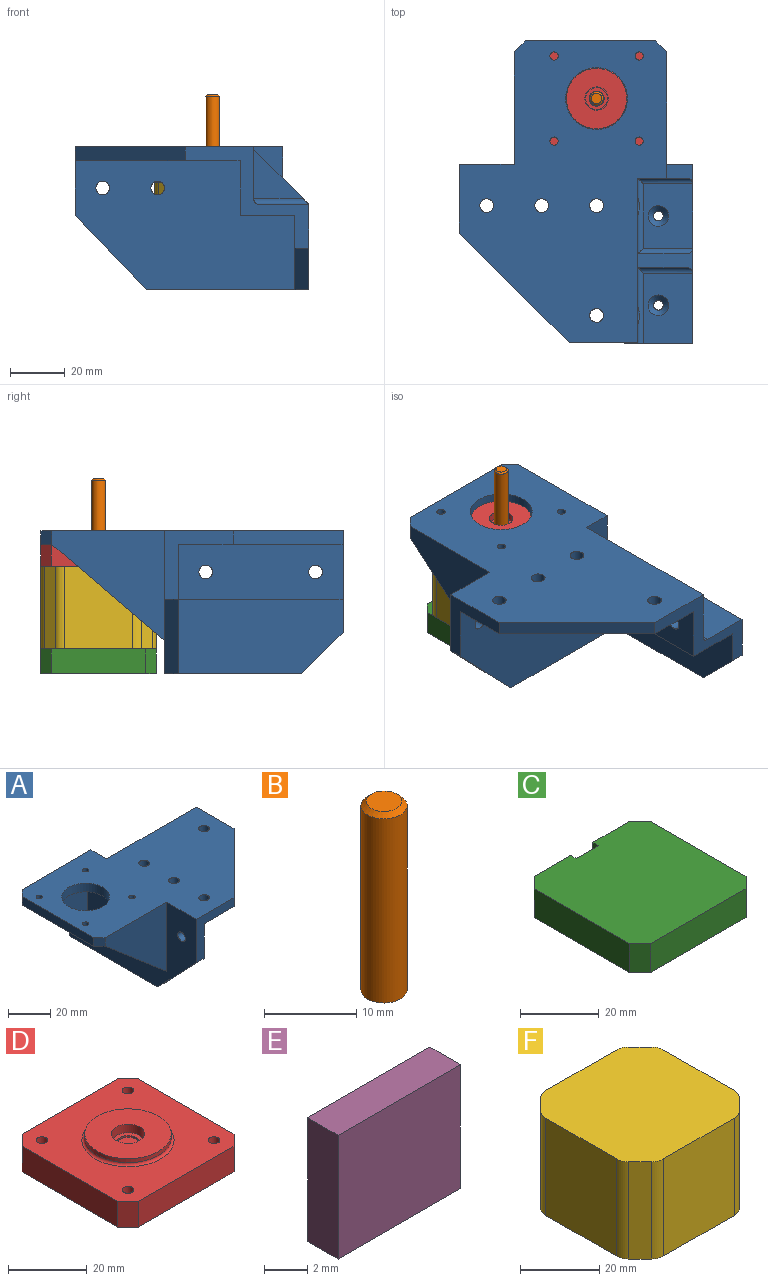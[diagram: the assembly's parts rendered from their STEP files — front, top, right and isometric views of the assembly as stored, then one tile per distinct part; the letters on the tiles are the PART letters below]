
ASSEMBLY  parts=6 mates=6
PART A: 56 faces, bbox 110x85x52 mm
  f0: cylinder r=2mm len=27.5mm, axis (1,0,0), area 73.4mm2, adj f6,f39,f49,f50,f54
  f1: cylinder r=2mm len=27.5mm, axis (1,0,0), area 75.7mm2, adj f3,f5,f6,f51,f53
  f2: plane 65x31mm, normal (0,1,0), area 1902.5mm2, adj f3,f5,f10,f24,f39,f41,f42,f52
  f3: plane 45x37mm, normal (1,0,0), area 365.9mm2, adj f1,f2,f4,f5,f6,f9,f21,f36
  f4: plane 60x27mm, normal (0,-1,0), area 1507.5mm2, adj f3,f8,f10,f38,f52
  f5: plane 25.5x18mm, normal (0,0,1), area 414.8mm2, adj f1,f2,f3,f48,f51
  f6: plane 60x20.5mm, normal (0,1,0), area 1026.3mm2, adj f0,f1,f3,f16,f21,f33,f37,f42
  f7: plane 46x40mm, normal (0,1,0), area 980mm2, adj f21,f24,f26,f32,f37,f41
  f8: plane 80x47mm, normal (1,0,0), area 2970.8mm2, adj f4,f9,f10,f11,f15,f17,f22,f36
  f9: plane 60x20mm, normal (0,-1,0), area 1160.7mm2, adj f3,f8,f16,f33,f36,f38
  f10: plane 59.08x50mm, normal (0,0,-1), area 520.4mm2, adj f2,f4,f8,f11,f24,f52
  f11: plane 27x25.92mm, normal (0,-0.72,-0.69), area 187.1mm2, adj f8,f10,f17,f24
  f12: plane 55.5x45mm, normal (0,0,-1), area 1809.6mm2, adj f13,f19,f23,f24,f25,f26,f27,f28
  f13: cylinder r=1.5mm len=5mm, axis (0,0,1), area 47.1mm2, adj f12,f21
  f14: cylinder r=2.5mm len=5mm, axis (0,0,1), area 78.5mm2, adj f21,f36
  f15: cylinder r=2.5mm len=5mm, axis (1,0,0), area 78.5mm2, adj f8,f24
  f16: cylinder r=2.5mm len=5mm, axis (0,-1,0), area 78.5mm2, adj f6,f9
  f17: plane 25x25mm, normal (0,-1,0), area 225mm2, adj f8,f11,f21,f24,f36,f40
  f18: plane 41x40mm, normal (0,-1,0), area 922.5mm2, adj f19,f21,f24,f31
  f19: plane 5x4mm, normal (-0.71,-0.71,0), area 28.3mm2, adj f12,f18,f21,f30
  f20: cylinder r=2.5mm len=5mm, axis (0,0,1), area 78.5mm2, adj f21,f36
  f21: plane 110x75.5mm, normal (0,0,1), area 5454.6mm2, adj f3,f6,f7,f13,f14,f17,f18,f19
  f22: cylinder r=2.5mm len=5mm, axis (1,0,0), area 78.5mm2, adj f8,f24
  f23: cylinder r=1.5mm len=5mm, axis (0,0,1), area 47.1mm2, adj f12,f21
  f24: plane 85x52mm, normal (-1,0,0), area 3388.9mm2, adj f2,f7,f10,f11,f12,f15,f17,f18
  f25: plane 41x35mm, normal (0,-1,0), area 717.5mm2, adj f12,f24,f32
  f26: plane 5x4mm, normal (-0.71,0.71,0), area 28.3mm2, adj f7,f12,f21,f30
  f27: cylinder r=11.25mm len=22.5mm, axis (0,0,1), area 353.4mm2, adj f12,f21
  f28: plane 41x35mm, normal (0,1,0), area 717.5mm2, adj f12,f24,f31
  f29: cylinder r=1.5mm len=5mm, axis (0,0,1), area 47.1mm2, adj f12,f21
  f30: plane 47.5x5mm, normal (-1,0,0), area 237.5mm2, adj f12,f19,f21,f26
  f31: plane 41x35mm, normal (-0.65,0,-0.76), area 161.7mm2, adj f12,f18,f24,f28
  f32: plane 41x35mm, normal (-0.65,0,-0.76), area 161.7mm2, adj f7,f12,f24,f25
  f33: cylinder r=2.5mm len=5mm, axis (0,-1,0), area 78.5mm2, adj f6,f9
  f34: cylinder r=2.5mm len=5mm, axis (0,0,1), area 78.5mm2, adj f21,f36
  f35: cylinder r=1.5mm len=5mm, axis (0,0,1), area 47.1mm2, adj f12,f21
  f36: plane 60x60mm, normal (0,0,-1), area 2721.5mm2, adj f3,f8,f9,f14,f17,f20,f34,f40
  f37: plane 19x18mm, normal (1,0,0), area 227.6mm2, adj f6,f7,f21,f41,f50
  f38: plane 60x20mm, normal (0,0,-1), area 1180.8mm2, adj f3,f4,f8,f9,f45,f46
  f39: plane 23.5x18mm, normal (0,0,1), area 378.8mm2, adj f0,f2,f47,f49,f50
  f40: plane 40x40mm, normal (0.71,-0.71,0), area 282.8mm2, adj f3,f17,f21,f36
  f41: plane 9.5x9.5mm, normal (0,0.71,0.71), area 68.4mm2, adj f2,f7,f24,f37,f50
  f42: plane 20x20mm, normal (0,0.71,0.71), area 143.8mm2, adj f2,f6,f43,f44,f49,f51
  f43: plane 18x18mm, normal (-1,0,0), area 162mm2, adj f6,f42,f49
  f44: plane 18x18mm, normal (1,0,0), area 162mm2, adj f6,f42,f51
  f45: cylinder r=1.75mm len=3.5mm, axis (0,0,1), area 22mm2, adj f38,f47
  f46: cylinder r=1.75mm len=3.5mm, axis (0,0,1), area 22mm2, adj f38,f48
  f47: cone r=1.75mm half-angle=45deg, axis (0,0,1), area 48.9mm2, adj f39,f45
  f48: cone r=1.75mm half-angle=45deg, axis (0,0,1), area 48.9mm2, adj f5,f46
  f49: cylinder r=2mm len=20mm, axis (0,1,0), area 58.3mm2, adj f0,f39,f42,f43
  f50: cylinder r=2mm len=20mm, axis (0,1,0), area 58.3mm2, adj f0,f37,f39,f41
  f51: cylinder r=2mm len=20mm, axis (0,-1,0), area 58.3mm2, adj f1,f5,f42,f44
  f52: plane 15x15mm, normal (0.71,0,-0.71), area 106.1mm2, adj f2,f3,f4,f10
  f53: cylinder r=5.5mm len=7.55mm, axis (0,-1,0), area 2.8mm2, adj f1,f6
  f54: cylinder r=5.5mm len=7.55mm, axis (0,-1,0), area 2.8mm2, adj f0,f6
  f55: cylinder r=2.5mm len=5mm, axis (0,0,1), area 78.5mm2, adj f21,f36
PART B: 4 faces, bbox 5x5x25 mm
  f0: cone r=1.93mm half-angle=45deg, axis (0,0,-1), area 11.3mm2, adj f1,f3
  f1: cylinder r=2.5mm len=24.43mm, axis (0,0,-1), area 383.7mm2, adj f0,f2
  f2: plane 5x5mm, normal (0,0,-1), area 19.6mm2, adj f1
  f3: plane 3.85x3.85mm, normal (0,0,1), area 11.6mm2, adj f0
PART C: 14 faces, bbox 42x42x9 mm
  f0: plane 34.37x9mm, normal (0,1,0), area 253.3mm2, adj f1,f7,f8,f9,f10,f11,f12
  f1: plane 9x3.82mm, normal (0.71,0.71,0), area 48.6mm2, adj f0,f2,f8,f9
  f2: plane 34.37x9mm, normal (1,0,0), area 309.3mm2, adj f1,f3,f8,f9
  f3: plane 9x3.82mm, normal (0.71,-0.71,0), area 48.6mm2, adj f2,f4,f8,f9
  f4: plane 34.37x9mm, normal (0,-1,0), area 309.3mm2, adj f3,f5,f8,f9
  f5: plane 9x3.82mm, normal (-0.71,-0.71,0), area 48.6mm2, adj f4,f6,f8,f9
  f6: plane 34.37x9mm, normal (-1,0,0), area 309.3mm2, adj f5,f7,f8,f9
  f7: plane 9x3.82mm, normal (-0.71,0.71,0), area 48.6mm2, adj f0,f6,f8,f9
  f8: plane 42x42mm, normal (0,0,-1), area 1734.9mm2, adj f0,f1,f2,f3,f4,f5,f6,f7
  f9: plane 42x42mm, normal (0,0,1), area 1718.9mm2, adj f0,f1,f2,f3,f4,f5,f6,f7
  f10: plane 7x2mm, normal (1,0,0), area 14mm2, adj f0,f9,f11,f13
  f11: plane 8x2mm, normal (0,0,1), area 16mm2, adj f0,f10,f12,f13
  f12: plane 7x2mm, normal (-1,0,0), area 14mm2, adj f0,f9,f11,f13
  f13: plane 8x7mm, normal (0,1,0), area 56mm2, adj f9,f10,f11,f12
PART D: 27 faces, bbox 42x42x10 mm
  f0: torus R=11.75mm, axis (0,0,-1), area 83.4mm2, adj f4,f18
  f1: cylinder r=2.75mm len=5.5mm, axis (0,0,-1), area 8.6mm2, adj f25,f26
  f2: cylinder r=4mm len=8mm, axis (0,0,-1), area 12.6mm2, adj f24,f25
  f3: cylinder r=4.25mm len=8.5mm, axis (0,0,1), area 80.1mm2, adj f23,f24
  f4: cylinder r=11mm len=22mm, axis (0,0,-1), area 86.4mm2, adj f0,f23
  f5: cylinder r=1.5mm len=4.5mm, axis (0,0,1), area 42.4mm2, adj f18,f22
  f6: cylinder r=1.5mm len=4.5mm, axis (0,0,1), area 42.4mm2, adj f18,f21
  f7: cylinder r=1.5mm len=4.5mm, axis (0,0,1), area 42.4mm2, adj f18,f20
  f8: cylinder r=1.5mm len=4.5mm, axis (0,0,1), area 42.4mm2, adj f18,f19
  f9: plane 8x3.82mm, normal (0.71,0.71,0), area 43.2mm2, adj f10,f16,f17,f18
  f10: plane 34.37x8mm, normal (1,0,0), area 274.9mm2, adj f9,f11,f17,f18
  f11: plane 8x3.82mm, normal (0.71,-0.71,0), area 43.2mm2, adj f10,f12,f17,f18
  f12: plane 34.37x8mm, normal (0,-1,0), area 274.9mm2, adj f11,f13,f17,f18
  f13: plane 8x3.82mm, normal (-0.71,-0.71,0), area 43.2mm2, adj f12,f14,f17,f18
  f14: plane 34.37x8mm, normal (-1,0,0), area 274.9mm2, adj f13,f15,f17,f18
  f15: plane 8x3.82mm, normal (-0.71,0.71,0), area 43.2mm2, adj f14,f16,f17,f18
  f16: plane 34.37x8mm, normal (0,1,0), area 274.9mm2, adj f9,f15,f17,f18
  f17: plane 42x42mm, normal (0,0,-1), area 1734.9mm2, adj f9,f10,f11,f12,f13,f14,f15,f16
  f18: plane 42x42mm, normal (0,0,1), area 1272.9mm2, adj f0,f5,f6,f7,f8,f9,f10,f11
  f19: plane 3x3mm, normal (0,0,1), area 7.1mm2, adj f8
  f20: plane 3x3mm, normal (0,0,1), area 7.1mm2, adj f7
  f21: plane 3x3mm, normal (0,0,1), area 7.1mm2, adj f6
  f22: plane 3x3mm, normal (0,0,1), area 7.1mm2, adj f5
  f23: plane 22x22mm, normal (0,0,1), area 323.4mm2, adj f3,f4
  f24: plane 8.5x8.5mm, normal (0,0,1), area 6.5mm2, adj f2,f3
  f25: plane 8x8mm, normal (0,0,1), area 26.5mm2, adj f1,f2
  f26: plane 5.5x5.5mm, normal (0,0,1), area 23.8mm2, adj f1
PART E: 11 faces, bbox 8x2x7 mm
  f0: plane 8x2mm, normal (0,0,-1), area 16mm2, adj f1,f3,f4,f9
  f1: plane 7x2mm, normal (-1,0,0), area 14mm2, adj f0,f2,f4,f9
  f2: plane 8x2mm, normal (0,0,1), area 16mm2, adj f1,f3,f4,f9
  f3: plane 7x2mm, normal (1,0,0), area 14mm2, adj f0,f2,f4,f9
  f4: plane 8x7mm, normal (0,-1,0), area 56mm2, adj f0,f1,f2,f3
  f5: plane 7.5x1.75mm, normal (0,0,-1), area 13.1mm2, adj f6,f8,f9,f10
  f6: plane 6.5x1.75mm, normal (-1,0,0), area 11.4mm2, adj f5,f7,f9,f10
  f7: plane 7.5x1.75mm, normal (0,0,1), area 13.1mm2, adj f6,f8,f9,f10
  f8: plane 6.5x1.75mm, normal (1,0,0), area 11.4mm2, adj f5,f7,f9,f10
  f9: plane 8x7mm, normal (0,1,0), area 7.3mm2, adj f0,f1,f2,f3,f5,f6,f7,f8
  f10: plane 7.5x6.5mm, normal (0,1,0), area 48.7mm2, adj f5,f6,f7,f8
PART F: 18 faces, bbox 42x42x30 mm
  f0: cylinder r=4.48mm len=30mm, axis (0,0,1), area 105.5mm2, adj f1,f15,f16,f17
  f1: plane 30x4.02mm, normal (0.71,-0.71,0), area 170.6mm2, adj f0,f2,f16,f17
  f2: cylinder r=4.48mm len=30mm, axis (0,0,1), area 105.5mm2, adj f1,f3,f16,f17
  f3: plane 30x25mm, normal (0,-1,0), area 750mm2, adj f2,f4,f16,f17
  f4: cylinder r=4.48mm len=30mm, axis (0,0,1), area 105.5mm2, adj f3,f5,f16,f17
  f5: plane 30x4.02mm, normal (-0.71,-0.71,0), area 170.6mm2, adj f4,f6,f16,f17
  f6: cylinder r=4.48mm len=30mm, axis (0,0,1), area 105.5mm2, adj f5,f7,f16,f17
  f7: plane 30x25mm, normal (-1,0,0), area 750mm2, adj f6,f8,f16,f17
  f8: cylinder r=4.48mm len=30mm, axis (0,0,1), area 105.5mm2, adj f7,f9,f16,f17
  f9: plane 30x4.02mm, normal (-0.71,0.71,0), area 170.6mm2, adj f8,f10,f16,f17
  f10: cylinder r=4.48mm len=30mm, axis (0,0,1), area 105.5mm2, adj f9,f11,f16,f17
  f11: plane 30x25mm, normal (0,1,0), area 750mm2, adj f10,f12,f16,f17
  f12: cylinder r=4.48mm len=30mm, axis (0,0,1), area 105.5mm2, adj f11,f13,f16,f17
  f13: plane 30x4.02mm, normal (0.71,0.71,0), area 170.6mm2, adj f12,f14,f16,f17
  f14: cylinder r=4.48mm len=30mm, axis (0,0,1), area 105.5mm2, adj f13,f15,f16,f17
  f15: plane 30x25mm, normal (1,0,0), area 750mm2, adj f0,f14,f16,f17
  f16: plane 42x42mm, normal (0,0,-1), area 1672.2mm2, adj f0,f1,f2,f3,f4,f5,f6,f7
  f17: plane 42x42mm, normal (0,0,1), area 1672.2mm2, adj f0,f1,f2,f3,f4,f5,f6,f7
PLACE A rot(axis=(0,0,-1),90deg) t=(0,-39,0)mm
PLACE B t=(0,0,0.07)mm
PLACE C at identity
PLACE D at identity fixed
PLACE E at identity
PLACE F at identity
MATE fastened F.f7 <-> C.f6  axis (-1,0,0) through (-21,0,-38)mm
MATE revolute B.f0 <-> D.f0  axis (0,0,1) through (0,0,23.5)mm
MATE fastened E.f9 <-> C.f0  axis (0,1,0) through (4,21,-45)mm
MATE revolute A.f35 <-> D.f7  axis (0,0,-1) through (15.5,15.5,0)mm
MATE fastened F.f7 <-> D.f14  axis (-1,0,0) through (-21,0,-8)mm
MATE revolute A.f29 <-> D.f5  axis (0,0,-1) through (-15.5,-15.5,0)mm
